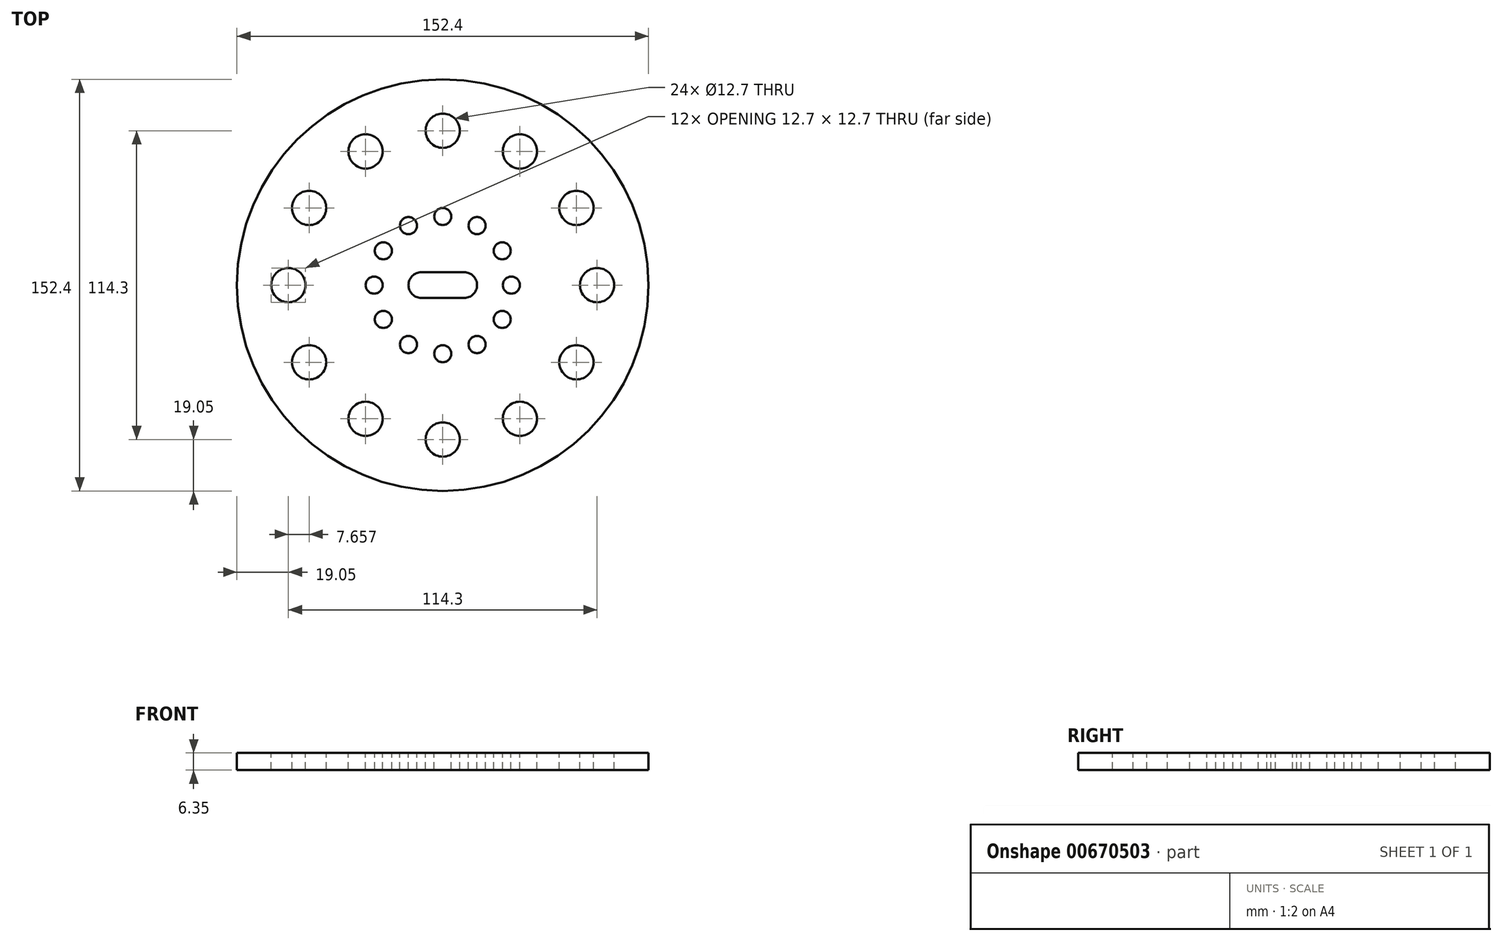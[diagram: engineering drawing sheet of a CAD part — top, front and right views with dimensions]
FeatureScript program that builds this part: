
annotation { "Feature Type Name" : "Feature", "Feature Type Description" : "" }
export const myFeature = defineFeature(function(context is Context, id is Id, definition is map)
    precondition{}
    {
        {
            var Q0;
            Q0=qCreatedBy(makeId("Front.planeOp"),FACE);
            var sketch = newSketch(context, id + "F0", { "sketchPlane" : qUnion([Q0])});
            skLineSegment(sketch, "E0.bottom", {"start": v(0, 0) * mm, "end": v(-76.2, 0) * mm});
            skLineSegment(sketch, "E0.top", {"start": v(0, 6.35) * mm, "end": v(-76.2, 6.35) * mm});
            skLineSegment(sketch, "E0.left", {"start": v(0, 0) * mm, "end": v(0, 6.35) * mm});
            skLineSegment(sketch, "E0.right", {"start": v(-76.2, 0) * mm, "end": v(-76.2, 6.35) * mm});
            skLineSegment(sketch, "E1.bottom", {"start": v(-76.2, 6.35) * mm, "end": v(-69.85, 6.35) * mm});
            skLineSegment(sketch, "E1.top", {"start": v(-76.2, 25.4) * mm, "end": v(-69.85, 25.4) * mm});
            skLineSegment(sketch, "E1.left", {"start": v(-76.2, 6.35) * mm, "end": v(-76.2, 25.4) * mm});
            skLineSegment(sketch, "E1.right", {"start": v(-69.85, 6.35) * mm, "end": v(-69.85, 25.4) * mm});
            skLineSegment(sketch, "E2.bottom", {"start": v(-38.1, 6.35) * mm, "end": v(-44.45, 6.35) * mm});
            skLineSegment(sketch, "E2.top", {"start": v(-38.1, 19.05) * mm, "end": v(-44.45, 19.05) * mm});
            skLineSegment(sketch, "E2.left", {"start": v(-38.1, 6.35) * mm, "end": v(-38.1, 19.05) * mm});
            skLineSegment(sketch, "E2.right", {"start": v(-44.45, 6.35) * mm, "end": v(-44.45, 19.05) * mm});
            skSolve(sketch);
        }
        {
            var Q0;
            Q0=makeQuery(id+"F0.imprint","IMPRINT",FACE,{"disambiguationData":[TD([[makeQuery(id+"F0.imprint","IMPRINT",EDGE,{"derivedFrom":sQuery(id+"F0.wireOp",EDGE,"E0.bottom")}),-1.0]])]});
            var Q1;
            Q1=makeQuery(id+"F0.imprint","IMPRINT",FACE,{"disambiguationData":[TD([[makeQuery(id+"F0.imprint","IMPRINT",EDGE,{"derivedFrom":sQuery(id+"F0.wireOp",EDGE,"E2.bottom")}),-1.0]])]});
            var Q2;
            Q2=makeQuery(id+"F0.imprint","IMPRINT",FACE,{"disambiguationData":[TD([[makeQuery(id+"F0.imprint","IMPRINT",EDGE,{"derivedFrom":sQuery(id+"F0.wireOp",EDGE,"E1.bottom")}),1.0]])]});
            var Q3;
            Q3=sQuery(id+"F0.wireOp",EDGE,"E0.left");
            revolve(context, id + "F1", {"entities" : qUnion([Q0, Q1, Q2]), "axis" : qUnion([Q3]), "revolveType" : RevolveType.FULL});
        }
        {
            var Q0;
            {var subQ0=sQuery(id+"F0.wireOp",EDGE,"E0.top");Q0=makeQuery(id+"F1.opRevolve","SWEPT_FACE",FACE,{"disambiguationData":[OSD([subQ0]),TDD([makeQuery(id+"F0.imprint","IMPRINT",EDGE,{"disambiguationData":[TD([[makeQuery(id+"F0.imprint","INTERSECT",VERTEX,{"derivedFrom":[subQ0,sQuery(id+"F0.wireOp",EDGE,"E1.bottom"),sQuery(id+"F0.wireOp",EDGE,"E1.right")]}),1.0]])],"derivedFrom":subQ0})])]});}
            var sketch = newSketch(context, id + "F2", { "sketchPlane" : qUnion([Q0])});
            skCircle(sketch, "E3", {"center": v(0, 0) * mm, "radius": 25.4 * mm, "construction": true});
            skCircle(sketch, "E4", {"center": v(0, 0) * mm, "radius": 57.15 * mm, "construction": true});
            skCircle(sketch, "E5", {"center": v(0, 57.15) * mm, "radius": 6.35 * mm});
            skCircle(sketch, "E6", {"center": v(0, 25.4) * mm, "radius": 3.18 * mm});
            skCircle(sketch, "E7.1.0", {"center": v(28.58, 49.5) * mm, "radius": 6.35 * mm});
            skCircle(sketch, "E7.1.1", {"center": v(12.7, 22) * mm, "radius": 3.18 * mm});
            skCircle(sketch, "E7.2.0", {"center": v(49.5, 28.57) * mm, "radius": 6.35 * mm});
            skCircle(sketch, "E7.2.1", {"center": v(22, 12.7) * mm, "radius": 3.18 * mm});
            skCircle(sketch, "E7.3.0", {"center": v(57.15, 0) * mm, "radius": 6.35 * mm});
            skCircle(sketch, "E7.3.1", {"center": v(25.4, 0) * mm, "radius": 3.18 * mm});
            skCircle(sketch, "E7.4.0", {"center": v(49.5, -28.58) * mm, "radius": 6.35 * mm});
            skCircle(sketch, "E7.4.1", {"center": v(22, -12.7) * mm, "radius": 3.18 * mm});
            skCircle(sketch, "E7.5.0", {"center": v(28.57, -49.5) * mm, "radius": 6.35 * mm});
            skCircle(sketch, "E7.5.1", {"center": v(12.7, -22) * mm, "radius": 3.18 * mm});
            skCircle(sketch, "E7.6.0", {"center": v(0, -57.15) * mm, "radius": 6.35 * mm});
            skCircle(sketch, "E7.6.1", {"center": v(0, -25.4) * mm, "radius": 3.18 * mm});
            skCircle(sketch, "E7.7.0", {"center": v(-28.57, -49.5) * mm, "radius": 6.35 * mm});
            skCircle(sketch, "E7.7.1", {"center": v(-12.7, -22) * mm, "radius": 3.18 * mm});
            skCircle(sketch, "E7.8.0", {"center": v(-49.5, -28.57) * mm, "radius": 6.35 * mm});
            skCircle(sketch, "E7.8.1", {"center": v(-22, -12.7) * mm, "radius": 3.18 * mm});
            skCircle(sketch, "E7.9.0", {"center": v(-57.15, 0) * mm, "radius": 6.35 * mm});
            skCircle(sketch, "E7.9.1", {"center": v(-25.4, 0) * mm, "radius": 3.18 * mm});
            skCircle(sketch, "E7.10.0", {"center": v(-49.5, 28.58) * mm, "radius": 6.35 * mm});
            skCircle(sketch, "E7.10.1", {"center": v(-22, 12.7) * mm, "radius": 3.18 * mm});
            skCircle(sketch, "E7.11.0", {"center": v(-28.57, 49.5) * mm, "radius": 6.35 * mm});
            skCircle(sketch, "E7.11.1", {"center": v(-12.7, 22) * mm, "radius": 3.18 * mm});
            skLineSegment(sketch, "E7.anchor1", {"start": v(0, 0) * mm, "end": v(0, 57.15) * mm, "construction": true});
            skLineSegment(sketch, "E7.anchor2", {"start": v(0, 0) * mm, "end": v(-28.57, 49.5) * mm, "construction": true});
            skLineSegment(sketch, "E8", {"start": v(0, 0) * mm, "end": v(-7.94, 0) * mm});
            skLineSegment(sketch, "E9", {"start": v(-7.94, 0) * mm, "end": v(7.94, 0) * mm});
            skArc(sketch, "E10.0.startCap", {"start": v(-7.94, -4.76) * mm, "mid": v(-12.7, 0) * mm, "end": v(-7.94, 4.76) * mm});
            skArc(sketch, "E10.0.endCap", {"start": v(7.94, 4.76) * mm, "mid": v(12.7, 0) * mm, "end": v(7.94, -4.76) * mm});
            skLineSegment(sketch, "E10.0.left", {"start": v(-7.94, 4.76) * mm, "end": v(7.94, 4.76) * mm});
            skLineSegment(sketch, "E10.0.right", {"start": v(-7.94, -4.76) * mm, "end": v(7.94, -4.76) * mm});
            skSolve(sketch);
        }
        {
            var Q0;
            Q0 = qSketchRegion(id + "F2", true);
            extrude(context, id + "F3", {"entities" : qUnion([Q0]), "operationType" : NewBodyOperationType.REMOVE, "endBound" : BoundingType.THROUGH_ALL, "oppositeDirection" : true, "depth" : 25.4 * mm, "offsetDistance" : 25.4 * mm});
        }
    });
